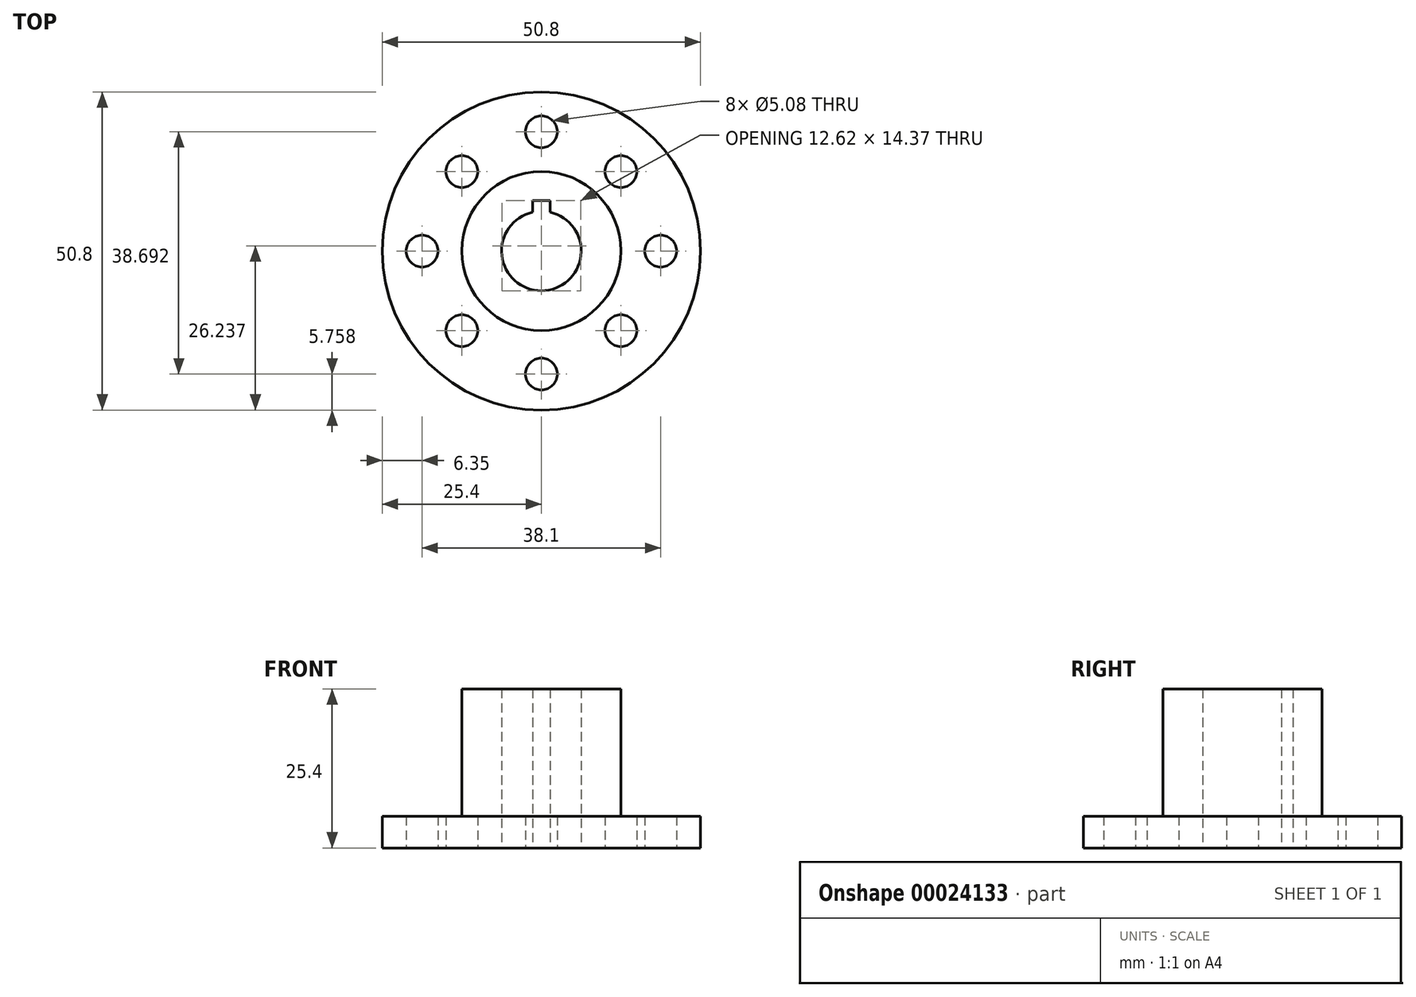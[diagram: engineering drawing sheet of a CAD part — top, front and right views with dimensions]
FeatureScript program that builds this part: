
annotation { "Feature Type Name" : "Feature", "Feature Type Description" : "" }
export const myFeature = defineFeature(function(context is Context, id is Id, definition is map)
    precondition{}
    {
        {
            var Q0;
            Q0=qCreatedBy(makeId("Top.planeOp"),FACE);
            var sketch = newSketch(context, id + "F0", { "sketchPlane" : qUnion([Q0])});
            skCircle(sketch, "E0", {"center": v(0, 0) * mm, "radius": 25.4 * mm});
            skCircle(sketch, "E1", {"center": v(0, 0) * mm, "radius": 12.7 * mm});
            skCircle(sketch, "E2", {"center": v(0, 0) * mm, "radius": 6.35 * mm});
            skLineSegment(sketch, "E3.rect.bottom", {"start": v(-1.4, 4.68) * mm, "end": v(1.4, 4.68) * mm});
            skLineSegment(sketch, "E3.rect.top", {"start": v(-1.4, 8.02) * mm, "end": v(1.4, 8.02) * mm});
            skLineSegment(sketch, "E3.rect.left", {"start": v(-1.4, 4.68) * mm, "end": v(-1.4, 8.02) * mm});
            skLineSegment(sketch, "E3.rect.right", {"start": v(1.4, 4.68) * mm, "end": v(1.4, 8.02) * mm});
            skPoint(sketch, "E3.rect.middle", {"position": v(0, 6.35) * mm});
            skLineSegment(sketch, "E4", {"start": v(0, 25.4) * mm, "end": v(0, 12.7) * mm, "construction": true});
            skLineSegment(sketch, "E5", {"start": v(12.7, 0) * mm, "end": v(25.4, 0) * mm, "construction": true});
            skLineSegment(sketch, "E6", {"start": v(-12.7, 0) * mm, "end": v(-25.4, 0) * mm, "construction": true});
            skLineSegment(sketch, "E7", {"start": v(0, -12.7) * mm, "end": v(0, -26.58) * mm, "construction": true});
            skCircle(sketch, "E8", {"center": v(-19.05, 0) * mm, "radius": 2.54 * mm});
            skCircle(sketch, "E9", {"center": v(0, 19.05) * mm, "radius": 2.54 * mm});
            skCircle(sketch, "E10", {"center": v(19.05, 0) * mm, "radius": 2.54 * mm});
            skCircle(sketch, "E11", {"center": v(0, -19.64) * mm, "radius": 2.54 * mm});
            skCircle(sketch, "E12", {"center": v(-12.7, -12.7) * mm, "radius": 2.54 * mm});
            skCircle(sketch, "E13", {"center": v(-12.7, 12.7) * mm, "radius": 2.54 * mm});
            skCircle(sketch, "E14", {"center": v(12.7, 12.7) * mm, "radius": 2.54 * mm});
            skCircle(sketch, "E15", {"center": v(12.7, -12.7) * mm, "radius": 2.54 * mm});
            skSolve(sketch);
        }
        {
            var Q0;
            Q0=makeQuery(id+"F0.imprint","IMPRINT",FACE,{"disambiguationData":[TD([[makeQuery(id+"F0.imprint","IMPRINT",EDGE,{"derivedFrom":sQuery(id+"F0.wireOp",EDGE,"E0")}),1.0]])]});
            extrude(context, id + "F1", {"entities" : qUnion([Q0]), "depth" : 5.08 * mm});
        }
        {
            var Q0;
            Q0=makeQuery(id+"F0.imprint","IMPRINT",FACE,{"disambiguationData":[TD([[makeQuery(id+"F0.imprint","IMPRINT",EDGE,{"derivedFrom":sQuery(id+"F0.wireOp",EDGE,"E1")}),1.0]])]});
            extrude(context, id + "F2", {"entities" : qUnion([Q0]), "operationType" : NewBodyOperationType.ADD, "depth" : 25.4 * mm});
        }
    });
